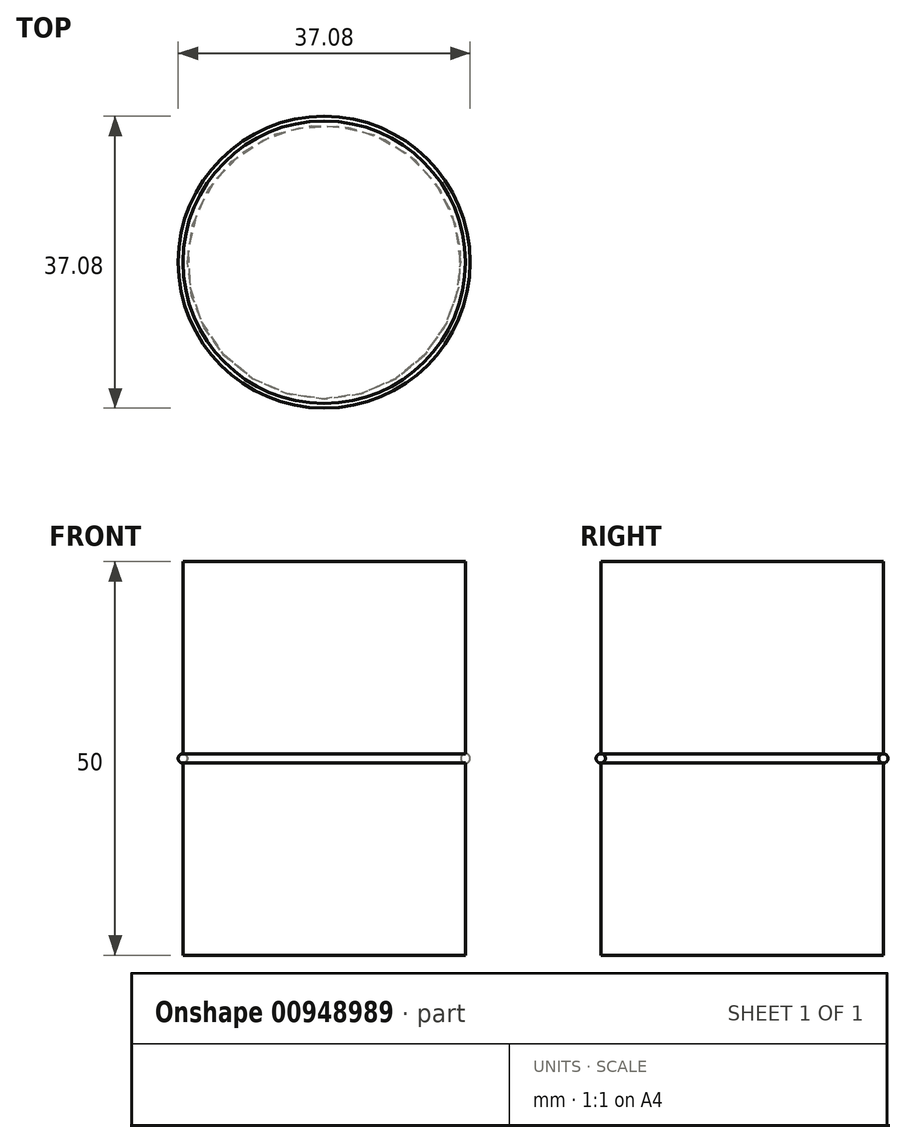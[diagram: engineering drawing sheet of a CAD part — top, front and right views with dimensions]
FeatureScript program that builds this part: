
annotation { "Feature Type Name" : "Feature", "Feature Type Description" : "" }
export const myFeature = defineFeature(function(context is Context, id is Id, definition is map)
    precondition{}
    {
        {
            var Q0;
            Q0=qCreatedBy(makeId("Top.planeOp"),FACE);
            var sketch = newSketch(context, id + "F0", { "sketchPlane" : qUnion([Q0])});
            skCircle(sketch, "E0", {"center": v(0, 0) * mm, "radius": 17.94 * mm});
            skSolve(sketch);
        }
        {
            var Q0;
            Q0=makeQuery(id+"F0.imprint","IMPRINT",FACE,{"disambiguationData":[TD([[makeQuery(id+"F0.imprint","IMPRINT",EDGE,{"derivedFrom":sQuery(id+"F0.wireOp",EDGE,"E0")}),1.0]])]});
            extrude(context, id + "F1", {"entities" : qUnion([Q0]), "endBound" : BoundingType.SYMMETRIC, "depth" : 50 * mm, "offsetDistance" : 25 * mm});
        }
        {
            var Q0;
            Q0=qCreatedBy(makeId("Front.planeOp"),FACE);
            var sketch = newSketch(context, id + "F2", { "sketchPlane" : qUnion([Q0])});
            skCircle(sketch, "E1", {"center": v(17.95, 0) * mm, "radius": 0.6 * mm});
            skLineSegment(sketch, "E2", {"start": v(0, 26.26) * mm, "end": v(0, -6) * mm});
            skSolve(sketch);
        }
        {
            var Q0;
            Q0=makeQuery(id+"F2.imprint","IMPRINT",FACE,{"disambiguationData":[TD([[makeQuery(id+"F2.imprint","IMPRINT",EDGE,{"derivedFrom":sQuery(id+"F2.wireOp",EDGE,"E1")}),1.0]])]});
            var Q1;
            Q1=sQuery(id+"F2.wireOp",EDGE,"E1");
            var Q2;
            Q2=sQuery(id+"F2.wireOp",EDGE,"E2");
            revolve(context, id + "F3", {"operationType" : NewBodyOperationType.REMOVE, "surfaceOperationType" : NewSurfaceOperationType.NEW, "entities" : qUnion([Q0]), "surfaceEntities" : qUnion([Q1]), "axis" : qUnion([Q2]), "revolveType" : RevolveType.FULL, "oppositeDirection" : true});
        }
        {
            var Q0;
            Q0=makeQuery(id+"F2.imprint","IMPRINT",FACE,{"disambiguationData":[TD([[makeQuery(id+"F2.imprint","IMPRINT",EDGE,{"derivedFrom":sQuery(id+"F2.wireOp",EDGE,"E1")}),1.0]])]});
            var Q1;
            Q1=sQuery(id+"F2.wireOp",EDGE,"E2");
            revolve(context, id + "F4", {"surfaceOperationType" : NewSurfaceOperationType.NEW, "entities" : qUnion([Q0]), "axis" : qUnion([Q1]), "revolveType" : RevolveType.FULL});
        }
    });
